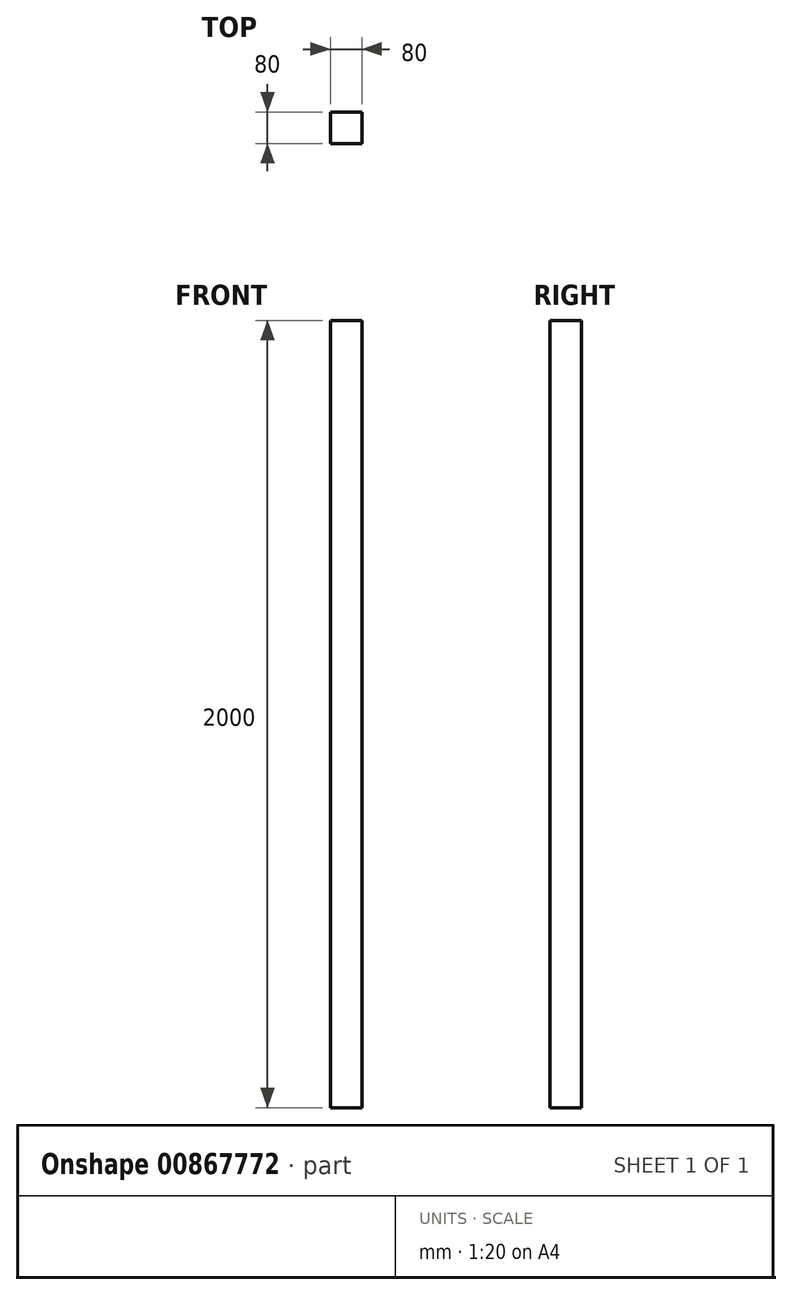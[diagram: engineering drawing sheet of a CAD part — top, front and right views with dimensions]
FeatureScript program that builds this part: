
annotation { "Feature Type Name" : "Feature", "Feature Type Description" : "" }
export const myFeature = defineFeature(function(context is Context, id is Id, definition is map)
    precondition{}
    {
        {
            var Q0;
            Q0=qCreatedBy(makeId("Top.planeOp"),FACE);
            var sketch = newSketch(context, id + "F0", { "sketchPlane" : qUnion([Q0])});
            skLineSegment(sketch, "E0.bottom", {"start": v(40, -40) * mm, "end": v(-40, -40) * mm});
            skLineSegment(sketch, "E0.top", {"start": v(40, 40) * mm, "end": v(-40, 40) * mm});
            skLineSegment(sketch, "E0.left", {"start": v(40, -40) * mm, "end": v(40, 40) * mm});
            skLineSegment(sketch, "E0.right", {"start": v(-40, -40) * mm, "end": v(-40, 40) * mm});
            skPoint(sketch, "E0.middle", {"position": v(0, 0) * mm});
            skSolve(sketch);
        }
        {
            var Q0;
            Q0=makeQuery(id+"F0.imprint","IMPRINT",FACE,{"disambiguationData":[TD([[makeQuery(id+"F0.imprint","IMPRINT",EDGE,{"derivedFrom":sQuery(id+"F0.wireOp",EDGE,"E0.bottom")}),-1.0]])]});
            extrude(context, id + "F1", {"entities" : qUnion([Q0]), "depth" : 2000 * mm, "offsetDistance" : 25 * mm});
        }
    });
